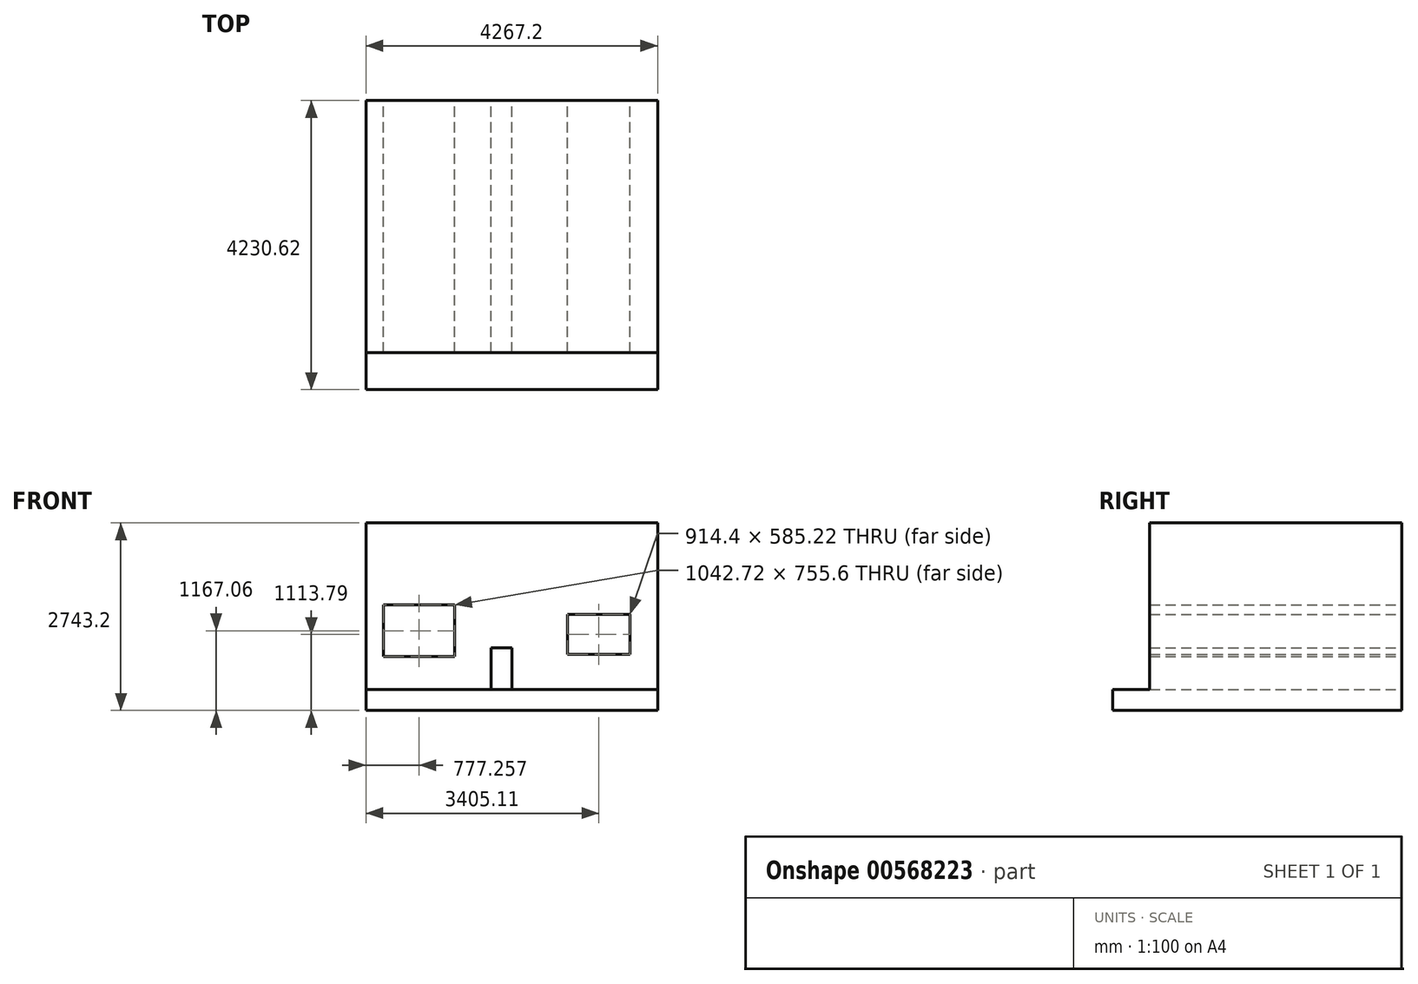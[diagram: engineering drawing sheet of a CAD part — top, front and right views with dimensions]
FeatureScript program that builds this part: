
annotation { "Feature Type Name" : "Feature", "Feature Type Description" : "" }
export const myFeature = defineFeature(function(context is Context, id is Id, definition is map)
    precondition{}
    {
        {
            var Q0;
            Q0=qCreatedBy(makeId("Front.planeOp"),FACE);
            var sketch = newSketch(context, id + "F0", { "sketchPlane" : qUnion([Q0])});
            skLineSegment(sketch, "E0", {"start": v(0, 0) * mm, "end": v(2133.6, 0) * mm});
            skLineSegment(sketch, "E1", {"start": v(0, 0) * mm, "end": v(-2133.6, 0) * mm});
            skLineSegment(sketch, "E2", {"start": v(0, 0) * mm, "end": v(0, 1219.2) * mm});
            skLineSegment(sketch, "E3", {"start": v(-2133.6, 0) * mm, "end": v(0, 1219.2) * mm});
            skLineSegment(sketch, "E4", {"start": v(0, 1219.2) * mm, "end": v(2133.6, 0) * mm});
            skLineSegment(sketch, "E5", {"start": v(-2133.6, 0) * mm, "end": v(-2438.4, 0) * mm});
            skLineSegment(sketch, "E6", {"start": v(2133.6, 0) * mm, "end": v(2438.4, 0) * mm});
            skLineSegment(sketch, "E7", {"start": v(0, 1219.2) * mm, "end": v(0, 1371.6) * mm});
            skLineSegment(sketch, "E8", {"start": v(0, 1371.6) * mm, "end": v(-2438.4, 0) * mm});
            skLineSegment(sketch, "E9", {"start": v(0, 1371.6) * mm, "end": v(2438.4, 0) * mm});
            skLineSegment(sketch, "E10", {"start": v(-2133.6, 0) * mm, "end": v(-2133.6, -2438.4) * mm});
            skPoint(sketch, "E11.start.orphan", {"position": v(2133.6, -2438.4) * mm});
            skLineSegment(sketch, "E12", {"start": v(-2133.6, -2438.4) * mm, "end": v(2133.6, -2438.4) * mm});
            skLineSegment(sketch, "E13", {"start": v(2133.6, -2438.4) * mm, "end": v(2133.6, 0) * mm});
            skLineSegment(sketch, "E14", {"start": v(-2133.6, -2438.4) * mm, "end": v(-2133.6, -2743.2) * mm});
            skLineSegment(sketch, "E15", {"start": v(-2133.6, -2743.2) * mm, "end": v(2133.6, -2743.2) * mm});
            skLineSegment(sketch, "E16", {"start": v(2133.6, -2743.2) * mm, "end": v(2133.6, -2438.4) * mm});
            skLineSegment(sketch, "E17", {"start": v(0, -2438.4) * mm, "end": v(-304.8, -2438.4) * mm});
            skLineSegment(sketch, "E18", {"start": v(0, -2438.4) * mm, "end": v(0, -1828.8) * mm});
            skLineSegment(sketch, "E19", {"start": v(0, -1828.8) * mm, "end": v(-304.8, -1828.8) * mm});
            skLineSegment(sketch, "E20", {"start": v(-304.8, -1828.8) * mm, "end": v(-304.8, -2438.4) * mm});
            skPoint(sketch, "E21", {"position": v(-112.12, -2133.6) * mm});
            skPoint(sketch, "E21.positionSnap0", {"position": v(0, -2133.6) * mm});
            skLineSegment(sketch, "E22.bottom", {"start": v(-1877.7, -1198.35) * mm, "end": v(-834.98, -1198.35) * mm});
            skLineSegment(sketch, "E22.top", {"start": v(-1877.7, -1953.94) * mm, "end": v(-834.98, -1953.94) * mm});
            skLineSegment(sketch, "E22.left", {"start": v(-1877.7, -1198.35) * mm, "end": v(-1877.7, -1953.94) * mm});
            skLineSegment(sketch, "E22.right", {"start": v(-834.98, -1198.35) * mm, "end": v(-834.98, -1953.94) * mm});
            skLineSegment(sketch, "E23.bottom", {"start": v(814.31, -1336.8) * mm, "end": v(1728.71, -1336.8) * mm});
            skLineSegment(sketch, "E23.top", {"start": v(814.31, -1922.02) * mm, "end": v(1728.71, -1922.02) * mm});
            skLineSegment(sketch, "E23.left", {"start": v(814.31, -1336.8) * mm, "end": v(814.31, -1922.02) * mm});
            skLineSegment(sketch, "E23.right", {"start": v(1728.71, -1336.8) * mm, "end": v(1728.71, -1922.02) * mm});
            skText(sketch, "E24", { "text": "Brendan F\'s", "fontName": "OpenSans-Regular.ttf"});
            const initialGuessF0  = {"E24": [-0.43064, 1.40849, 1, 0, 0.56395]};
            skSetInitialGuess(sketch, initialGuessF0);
            skSolve(sketch);
        }
        {
            var Q0;
            {var subQ0=sQuery(id+"F0.wireOp",EDGE,"E14");Q0=makeQuery(id+"F0.imprint","IMPRINT",FACE,{"disambiguationData":[TD([[makeQuery(id+"F0.imprint","IMPRINT",EDGE,{"derivedFrom":subQ0}),1.0]])]});}
            extrude(context, id + "F1", {"entities" : qUnion([Q0]), "depth" : 4230.62 * mm, "offsetDistance" : 30.48 * mm});
        }
        {
            var Q0;
            Q0=makeQuery(id+"F0.imprint","IMPRINT",FACE,{"disambiguationData":[TD([[makeQuery(id+"F0.imprint","IMPRINT",EDGE,{"derivedFrom":sQuery(id+"F0.wireOp",EDGE,"E0")}),-1.0]])]});
            extrude(context, id + "F2", {"entities" : qUnion([Q0]), "operationType" : NewBodyOperationType.ADD, "depth" : 3688.08 * mm, "offsetDistance" : 30.48 * mm});
        }
    });
